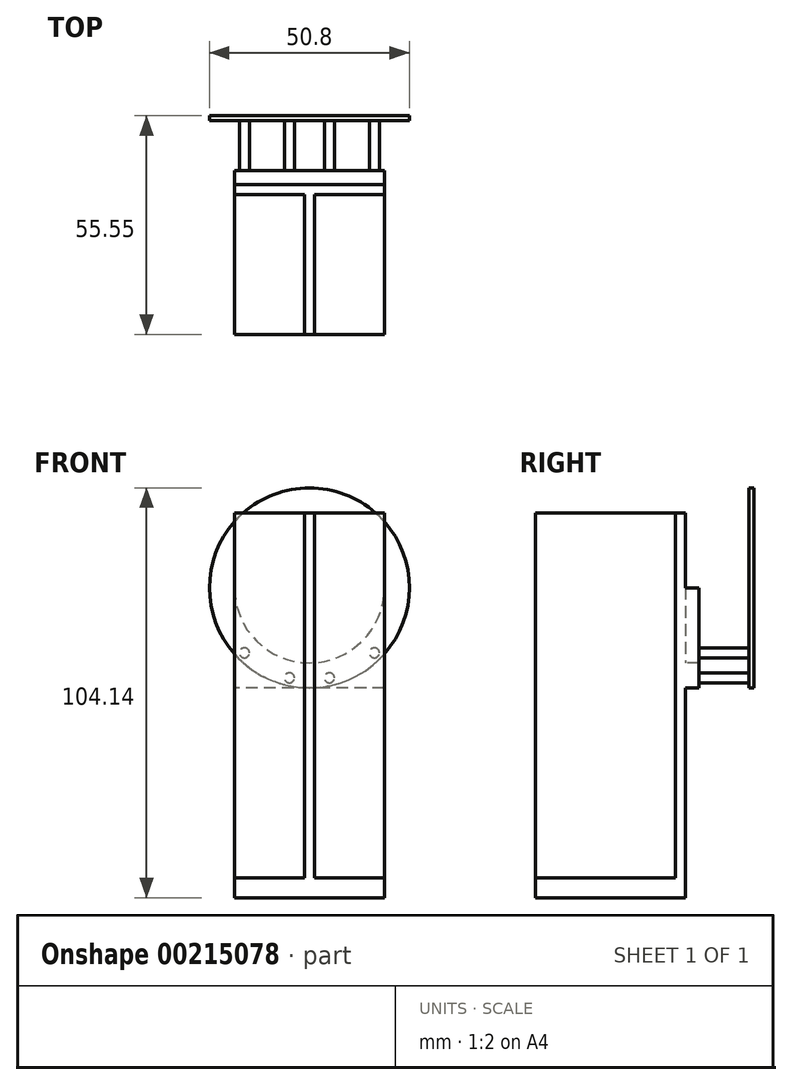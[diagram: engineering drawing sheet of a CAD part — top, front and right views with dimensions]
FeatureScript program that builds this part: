
annotation { "Feature Type Name" : "Feature", "Feature Type Description" : "" }
export const myFeature = defineFeature(function(context is Context, id is Id, definition is map)
    precondition{}
    {
        {
            var Q0;
            Q0=qCreatedBy(makeId("Top.planeOp"),FACE);
            var sketch = newSketch(context, id + "F0", { "sketchPlane" : qUnion([Q0])});
            skLineSegment(sketch, "E0.bottom", {"start": v(19.05, 19.05) * mm, "end": v(-19.05, 19.05) * mm});
            skLineSegment(sketch, "E0.top", {"start": v(19.05, -19.05) * mm, "end": v(-19.05, -19.05) * mm});
            skLineSegment(sketch, "E0.left", {"start": v(19.05, 19.05) * mm, "end": v(19.05, -19.05) * mm});
            skLineSegment(sketch, "E0.right", {"start": v(-19.05, 19.05) * mm, "end": v(-19.05, -19.05) * mm});
            skPoint(sketch, "E0.middle", {"position": v(0, 0) * mm});
            skSolve(sketch);
        }
        {
            var Q0;
            Q0 = qSketchRegion(id + "F0", true);
            extrude(context, id + "F1", {"entities" : qUnion([Q0]), "depth" : 5.08 * mm});
        }
        {
            var Q0;
            Q0=makeQuery(id+"F1.opExtrude","CAP_FACE",FACE,{"disambiguationData":[OSD([sQuery(id+"F0.wireOp",EDGE,"E0.bottom"),sQuery(id+"F0.wireOp",EDGE,"E0.top"),sQuery(id+"F0.wireOp",EDGE,"E0.left"),sQuery(id+"F0.wireOp",EDGE,"E0.right")])],"isStart":false});
            var sketch = newSketch(context, id + "F2", { "sketchPlane" : qUnion([Q0])});
            skLineSegment(sketch, "E1.bottom", {"start": v(1.27, 19.05) * mm, "end": v(-1.27, 19.05) * mm});
            skLineSegment(sketch, "E1.top", {"start": v(1.27, -19.05) * mm, "end": v(-1.27, -19.05) * mm});
            skLineSegment(sketch, "E1.left", {"start": v(1.27, 16.51) * mm, "end": v(1.27, -19.05) * mm});
            skLineSegment(sketch, "E1.right", {"start": v(-1.27, 16.51) * mm, "end": v(-1.27, -19.05) * mm});
            skPoint(sketch, "E1.middle", {"position": v(0, 0) * mm});
            skLineSegment(sketch, "E2.bottom", {"start": v(-19.05, 19.05) * mm, "end": v(19.05, 19.05) * mm});
            skLineSegment(sketch, "E2.top", {"start": v(-19.05, 16.51) * mm, "end": v(-1.27, 16.51) * mm});
            skLineSegment(sketch, "E2.left", {"start": v(-19.05, 19.05) * mm, "end": v(-19.05, 16.51) * mm});
            skLineSegment(sketch, "E2.right", {"start": v(19.05, 19.05) * mm, "end": v(19.05, 16.51) * mm});
            skLineSegment(sketch, "E3.trimOffspring", {"start": v(1.27, 16.51) * mm, "end": v(19.05, 16.51) * mm});
            skSolve(sketch);
        }
        {
            var Q0;
            Q0 = qSketchRegion(id + "F2", true);
            extrude(context, id + "F3", {"entities" : qUnion([Q0]), "operationType" : NewBodyOperationType.ADD, "depth" : 92.7 * mm});
        }
        {
            var Q0;
            Q0=makeQuery(id+"F3.boolean.opBoolean","MERGE",FACE,{"derivedFrom":[makeQuery(id+"F1.opExtrude","SWEPT_FACE",FACE,{"disambiguationData":[OSD([sQuery(id+"F0.wireOp",EDGE,"E0.bottom")])]}),makeQuery(id+"F3.opExtrude","SWEPT_FACE",FACE,{"disambiguationData":[OSD([sQuery(id+"F2.wireOp",EDGE,"E2.bottom")])]})]});
            var sketch = newSketch(context, id + "F4", { "sketchPlane" : qUnion([Q0])});
            skArc(sketch, "E4", {"start": v(-19.05, 78.74) * mm, "mid": v(0, 59.7) * mm, "end": v(19.05, 78.74) * mm});
            skPoint(sketch, "E5", {"position": v(0, 59.7) * mm});
            skPoint(sketch, "E6", {"position": v(-19.05, 59.7) * mm});
            skPoint(sketch, "E7", {"position": v(19.05, 59.7) * mm});
            skLineSegment(sketch, "E8", {"start": v(-19.05, 78.74) * mm, "end": v(-19.05, 59.7) * mm});
            skLineSegment(sketch, "E9", {"start": v(19.05, 59.7) * mm, "end": v(19.05, 78.74) * mm});
            skLineSegment(sketch, "E10", {"start": v(-19.05, 59.7) * mm, "end": v(-19.05, 53.34) * mm});
            skLineSegment(sketch, "E11", {"start": v(-19.05, 53.34) * mm, "end": v(19.05, 53.34) * mm});
            skLineSegment(sketch, "E12", {"start": v(19.05, 53.34) * mm, "end": v(19.05, 59.7) * mm});
            skSolve(sketch);
        }
        {
            var Q0;
            Q0=makeQuery(id+"F4.imprint","IMPRINT",FACE,{"disambiguationData":[TD([[makeQuery(id+"F4.imprint","IMPRINT",EDGE,{"derivedFrom":sQuery(id+"F4.wireOp",EDGE,"E4")}),-1.0]])]});
            extrude(context, id + "F5", {"entities" : qUnion([Q0]), "operationType" : NewBodyOperationType.ADD, "depth" : 3.48 * mm});
        }
        {
            var Q0;
            Q0=makeQuery(id+"F5.opExtrude","CAP_FACE",FACE,{"disambiguationData":[OSD([sQuery(id+"F4.wireOp",EDGE,"E4"),sQuery(id+"F4.wireOp",EDGE,"E8"),sQuery(id+"F4.wireOp",EDGE,"E9"),sQuery(id+"F4.wireOp",EDGE,"E10"),sQuery(id+"F4.wireOp",EDGE,"E11"),sQuery(id+"F4.wireOp",EDGE,"E12")])],"isStart":false});
            cPlane(context, id + "F6", {"entities" : qUnion([Q0]), "cplaneType" : CPlaneType.OFFSET, "offset" : 12.7 * mm, "width" : 152.4 * mm, "height" : 152.4 * mm});
        }
        {
            var Q0;
            Q0=qCreatedBy(id+"F6.planeOp",FACE);
            var sketch = newSketch(context, id + "F7", { "sketchPlane" : qUnion([Q0])});
            skCircle(sketch, "E13", {"center": v(0, 78.74) * mm, "radius": 19.05 * mm, "construction": true});
            skCircle(sketch, "E14", {"center": v(0, 78.74) * mm, "radius": 25.4 * mm});
            skSolve(sketch);
        }
        {
            var Q0;
            Q0 = qSketchRegion(id + "F7", true);
            extrude(context, id + "F8", {"entities" : qUnion([Q0]), "depth" : 1.27 * mm});
        }
        {
            var Q0;
            Q0=makeQuery(id+"F5.opExtrude","CAP_FACE",FACE,{"disambiguationData":[OSD([sQuery(id+"F4.wireOp",EDGE,"E4"),sQuery(id+"F4.wireOp",EDGE,"E8"),sQuery(id+"F4.wireOp",EDGE,"E9"),sQuery(id+"F4.wireOp",EDGE,"E10"),sQuery(id+"F4.wireOp",EDGE,"E11"),sQuery(id+"F4.wireOp",EDGE,"E12")])],"isStart":false});
            var sketch = newSketch(context, id + "F9", { "sketchPlane" : qUnion([Q0])});
            skCircle(sketch, "E15", {"center": v(-5.08, 55.88) * mm, "radius": 1.27 * mm});
            skCircle(sketch, "E16", {"center": v(5.08, 55.88) * mm, "radius": 1.27 * mm});
            skCircle(sketch, "E17", {"center": v(-16.51, 62.23) * mm, "radius": 1.27 * mm});
            skCircle(sketch, "E18", {"center": v(16.51, 62.23) * mm, "radius": 1.27 * mm});
            skSolve(sketch);
        }
        {
            var Q0;
            Q0 = qSketchRegion(id + "F9", true);
            var Q1;
            Q1=makeQuery(id+"F8.opExtrude","CAP_FACE",FACE,{"disambiguationData":[OSD([sQuery(id+"F7.wireOp",EDGE,"E14")])],"isStart":true});
            extrude(context, id + "F10", {"entities" : qUnion([Q0]), "endBound" : BoundingType.UP_TO_SURFACE, "endBoundEntityFace" : qUnion([Q1]), "depth" : 25.4 * mm});
        }
    });
